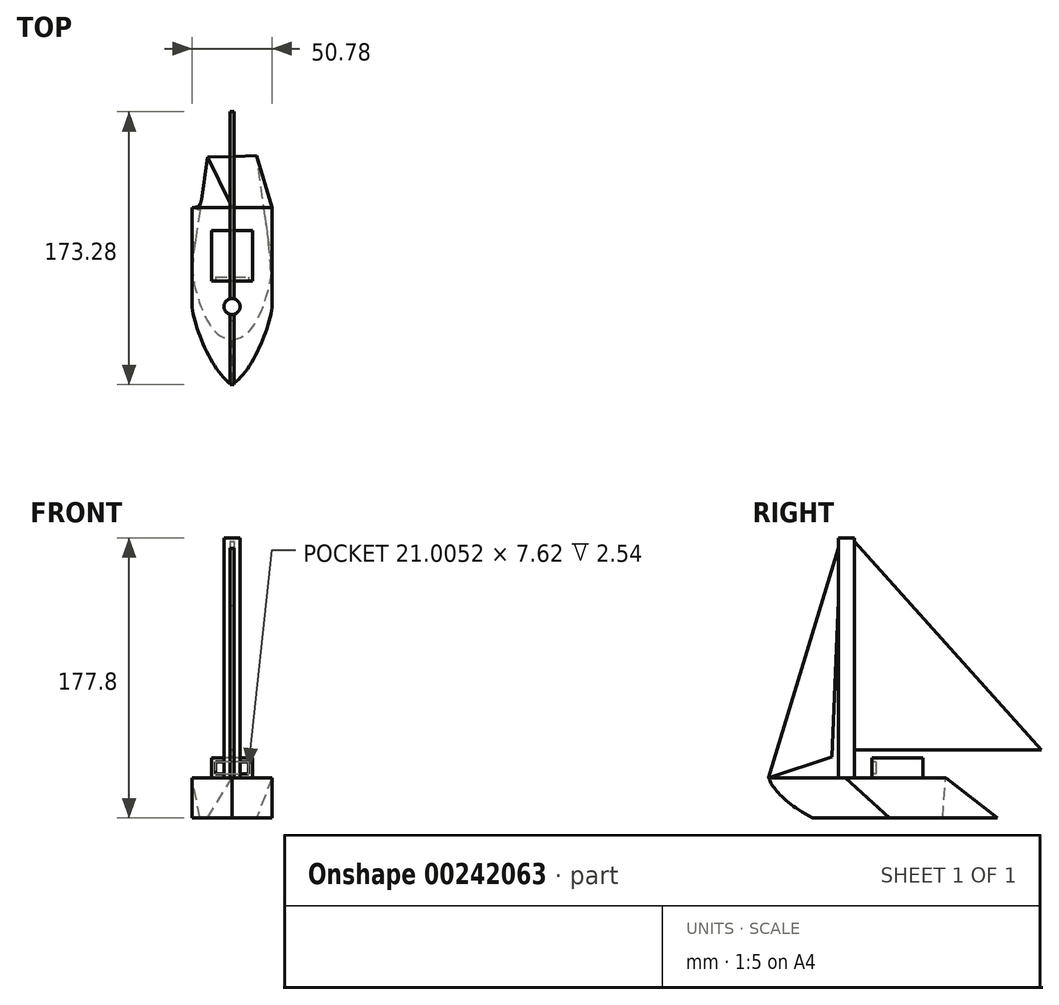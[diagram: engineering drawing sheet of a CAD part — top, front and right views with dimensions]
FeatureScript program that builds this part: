
annotation { "Feature Type Name" : "Feature", "Feature Type Description" : "" }
export const myFeature = defineFeature(function(context is Context, id is Id, definition is map)
    precondition{}
    {
        {
            var Q0;
            Q0=qCreatedBy(makeId("Top.planeOp"),FACE);
            var sketch = newSketch(context, id + "F0", { "sketchPlane" : qUnion([Q0])});
            skLineSegment(sketch, "E0", {"start": v(0, 46.92) * mm, "end": v(-25.39, 46.92) * mm});
            skLineSegment(sketch, "E1", {"start": v(-25.39, 46.92) * mm, "end": v(-25.39, -16.69) * mm});
            skFitSpline(sketch, "E2", {"points": [v(-25.39, -16.69) * mm, v(0, -65.46) * mm], "startDerivative": vector(6, -46.2) * mm, "endDerivative": vector(34.23, -18.83) * mm});
            skFitSpline(sketch, "E3.MirrorCS", {"points": [v(25.39, -16.69) * mm, v(0, -65.46) * mm], "startDerivative": vector(-6, -46.2) * mm, "endDerivative": vector(-34.23, -18.83) * mm});
            skLineSegment(sketch, "E4.MirrorCS", {"start": v(0, 46.92) * mm, "end": v(25.39, 46.92) * mm});
            skLineSegment(sketch, "E5.MirrorCS", {"start": v(25.39, 46.92) * mm, "end": v(25.39, -16.69) * mm});
            skSolve(sketch);
        }
        {
            var Q0;
            Q0=qCreatedBy(makeId("Top.planeOp"),FACE);
            cPlane(context, id + "F1", {"entities" : qUnion([Q0]), "cplaneType" : CPlaneType.OFFSET, "offset" : 25.4 * mm, "oppositeDirection" : true, "width" : 152.4 * mm, "height" : 152.4 * mm});
        }
        {
            var Q0;
            Q0=qCreatedBy(id+"F1.planeOp",FACE);
            var sketch = newSketch(context, id + "F2", { "sketchPlane" : qUnion([Q0])});
            skLineSegment(sketch, "E6.0.0", {"start": v(25.39, 11.24) * mm, "end": v(15.62, 79.73) * mm});
            skLineSegment(sketch, "E6.0.3", {"start": v(-15.47, 78.88) * mm, "end": v(-25.39, 11.24) * mm});
            skFitSpline(sketch, "E6.0.4", {"points": [v(-25.39, 11.24) * mm, v(-23.39, -4.17) * mm, v(-11.4, -31.26) * mm, v(0, -37.54) * mm]});
            skFitSpline(sketch, "E6.0.5", {"points": [v(0, -37.54) * mm, v(11.4, -31.26) * mm, v(23.39, -4.17) * mm, v(25.39, 11.24) * mm]});
            skLineSegment(sketch, "E7", {"start": v(-15.47, 78.88) * mm, "end": v(15.62, 79.73) * mm});
            skSolve(sketch);
        }
        {
            var Q0;
            Q0=qCreatedBy(makeId("Right.planeOp"),FACE);
            var sketch = newSketch(context, id + "F3", { "sketchPlane" : qUnion([Q0])});
            skFitSpline(sketch, "E8", {"points": [v(-65.46, 0) * mm, v(-37.54, -25.4) * mm], "startDerivative": vector(6, -17.03) * mm, "endDerivative": vector(55.16, -28.17) * mm});
            skSolve(sketch);
        }
        {
            var Q0;
            Q0=sQuery(id+"F0.wireOp",VERTEX,"E5.MirrorCS.start");
            var Q1;
            Q1=sQuery(id+"F2.wireOp",VERTEX,"E6.0.0.end");
            var Q2;
            Q2=sQuery(id+"F0.wireOp",VERTEX,"E0.end");
            cPlane(context, id + "F4", {"entities" : qUnion([Q0, Q1, Q2]), "cplaneType" : CPlaneType.THREE_POINT, "offset" : 25.4 * mm, "width" : 152.4 * mm, "height" : 152.4 * mm});
        }
        {
            var Q0;
            Q0=qCreatedBy(id+"F4.planeOp",FACE);
            var sketch = newSketch(context, id + "F5", { "sketchPlane" : qUnion([Q0])});
            skLineSegment(sketch, "E9", {"start": v(25.39, -37.1) * mm, "end": v(15.62, -78.6) * mm});
            skSolve(sketch);
        }
        {
            var Q0;
            Q0=makeQuery(id+"F2.imprint","IMPRINT",FACE,{"disambiguationData":[TD([[makeQuery(id+"F2.imprint","IMPRINT",EDGE,{"derivedFrom":sQuery(id+"F2.wireOp",EDGE,"E6.0.0")}),1.0]])]});
            var Q1;
            Q1=makeQuery(id+"F0.imprint","IMPRINT",FACE,{"disambiguationData":[TD([[makeQuery(id+"F0.imprint","IMPRINT",EDGE,{"derivedFrom":sQuery(id+"F0.wireOp",EDGE,"E0")}),1.0]])]});
            var Q2;
            Q2=sQuery(id+"F5.wireOp",EDGE,"E9");
            var Q3;
            Q3=sQuery(id+"F3.wireOp",EDGE,"E8");
            loft(context, id + "F6", {"addGuides" : true, "sheetProfilesArray" : [{ "sheetProfileEntities" : qUnion([Q0]) }, { "sheetProfileEntities" : qUnion([Q1]) }], "guidesArray" : [{ "guideEntities" : qUnion([Q2]), "guideDerivativeType" : LoftGuideDerivativeType.DEFAULT, "guideDerivativeMagnitude" : 1 }, { "guideEntities" : qUnion([Q3]), "guideDerivativeType" : LoftGuideDerivativeType.DEFAULT, "guideDerivativeMagnitude" : 1 }]});
        }
        {
            var Q0;
            Q0=makeQuery(id+"F6.opLoft","CAP_FACE",FACE,{"disambiguationData":[OSD([makeQuery(id+"F0.imprint","IMPRINT",FACE,{"disambiguationData":[TD([[makeQuery(id+"F0.imprint","IMPRINT",EDGE,{"derivedFrom":sQuery(id+"F0.wireOp",EDGE,"E0")}),1.0]])]})])],"isStart":true});
            var sketch = newSketch(context, id + "F7", { "sketchPlane" : qUnion([Q0])});
            skSolve(sketch);
        }
        {
            var Q0;
            {var subQ5=sQuery(id+"F0.wireOp",EDGE,"E0");var subQ6=sQuery(id+"F5.wireOp",EDGE,"E9");Q0=makeQuery(id+"F7.imprint","IMPRINT",FACE,{"disambiguationData":[TD([[makeQuery(id+"F7.imprint","IMPRINT",EDGE,{"derivedFrom":makeQuery(id+"F6.opLoft","MID_CAP_EDGE",EDGE,{"disambiguationData":[OSD([subQ5,sQuery(id+"F0.wireOp",EDGE,"E4.MirrorCS"),subQ6])],"capPos":1.0})}),1.0]])]});}
            var sketch = newSketch(context, id + "F8", { "sketchPlane" : qUnion([Q0])});
            skLineSegment(sketch, "E10", {"start": v(0, 0) * mm, "end": v(-13.04, 0) * mm});
            skLineSegment(sketch, "E11", {"start": v(-13.04, 0) * mm, "end": v(-13.04, 32.38) * mm});
            skLineSegment(sketch, "E12", {"start": v(-13.04, 32.38) * mm, "end": v(0, 32.38) * mm});
            skLineSegment(sketch, "E13.MirrorCS", {"start": v(13.04, 0) * mm, "end": v(13.04, 32.38) * mm});
            skLineSegment(sketch, "E14.MirrorCS", {"start": v(13.04, 32.38) * mm, "end": v(0, 32.38) * mm});
            skLineSegment(sketch, "E15.MirrorCS", {"start": v(0, 0) * mm, "end": v(13.04, 0) * mm});
            skSolve(sketch);
        }
        {
            var Q0;
            Q0 = qSketchRegion(id + "F8", true);
            extrude(context, id + "F9", {"entities" : qUnion([Q0]), "operationType" : NewBodyOperationType.ADD, "depth" : 12.7 * mm});
        }
        {
            var Q0;
            {var subQ5=sQuery(id+"F0.wireOp",EDGE,"E0");var subQ6=sQuery(id+"F5.wireOp",EDGE,"E9");Q0=makeQuery(id+"F7.imprint","IMPRINT",FACE,{"disambiguationData":[TD([[makeQuery(id+"F7.imprint","IMPRINT",EDGE,{"derivedFrom":makeQuery(id+"F6.opLoft","MID_CAP_EDGE",EDGE,{"disambiguationData":[OSD([subQ5,sQuery(id+"F0.wireOp",EDGE,"E4.MirrorCS"),subQ6])],"capPos":1.0})}),1.0]])]});}
            var sketch = newSketch(context, id + "F10", { "sketchPlane" : qUnion([Q0])});
            skCircle(sketch, "E16", {"center": v(0, -16.07) * mm, "radius": 5.12 * mm});
            skSolve(sketch);
        }
        {
            var Q0;
            Q0=makeQuery(id+"F10.imprint","IMPRINT",FACE,{"disambiguationData":[TD([[makeQuery(id+"F10.imprint","IMPRINT",EDGE,{"derivedFrom":sQuery(id+"F10.wireOp",EDGE,"E16")}),1.0]])]});
            extrude(context, id + "F11", {"entities" : qUnion([Q0]), "operationType" : NewBodyOperationType.ADD, "depth" : 152.4 * mm});
        }
        {
            var Q0;
            Q0=qCreatedBy(makeId("Right.planeOp"),FACE);
            var sketch = newSketch(context, id + "F12", { "sketchPlane" : qUnion([Q0])});
            skLineSegment(sketch, "E17", {"start": v(-19.34, 151.7) * mm, "end": v(-25.33, 13.5) * mm});
            skLineSegment(sketch, "E18", {"start": v(-25.33, 13.5) * mm, "end": v(-65.55, 0) * mm});
            skLineSegment(sketch, "E19", {"start": v(-65.55, 0) * mm, "end": v(-19.34, 151.7) * mm});
            skLineSegment(sketch, "E20", {"start": v(-12.5, 151.7) * mm, "end": v(107.73, 17.78) * mm});
            skLineSegment(sketch, "E21", {"start": v(107.73, 17.78) * mm, "end": v(-11.21, 17.78) * mm});
            skLineSegment(sketch, "E22", {"start": v(-11.21, 17.78) * mm, "end": v(-12.5, 151.7) * mm});
            skSolve(sketch);
        }
        {
            var Q0;
            Q0=makeQuery(id+"F12.imprint","IMPRINT",FACE,{"disambiguationData":[TD([[makeQuery(id+"F12.imprint","IMPRINT",EDGE,{"derivedFrom":sQuery(id+"F12.wireOp",EDGE,"E17")}),-1.0]])]});
            var Q1;
            Q1=makeQuery(id+"F12.imprint","IMPRINT",FACE,{"disambiguationData":[TD([[makeQuery(id+"F12.imprint","IMPRINT",EDGE,{"derivedFrom":sQuery(id+"F12.wireOp",EDGE,"E20")}),-1.0]])]});
            extrude(context, id + "F13", {"entities" : qUnion([Q0, Q1]), "operationType" : NewBodyOperationType.ADD, "endBound" : BoundingType.SYMMETRIC, "depth" : 2.54 * mm});
        }
        {
            var Q0;
            Q0=makeQuery(id+"F9.opExtrude","SWEPT_FACE",FACE,{"disambiguationData":[OSD([sQuery(id+"F8.wireOp",EDGE,"E10"),sQuery(id+"F8.wireOp",EDGE,"E15.MirrorCS")])]});
            var sketch = newSketch(context, id + "F14", { "sketchPlane" : qUnion([Q0])});
            skLineSegment(sketch, "E23.0", {"start": v(-10.5, 2.54) * mm, "end": v(10.5, 2.54) * mm});
            skLineSegment(sketch, "E23.1", {"start": v(-10.5, 10.16) * mm, "end": v(-10.5, 2.54) * mm});
            skLineSegment(sketch, "E23.2", {"start": v(10.5, 10.16) * mm, "end": v(-10.5, 10.16) * mm});
            skLineSegment(sketch, "E23.3", {"start": v(10.5, 2.54) * mm, "end": v(10.5, 10.16) * mm});
            skSolve(sketch);
        }
        {
            var Q0;
            Q0=makeQuery(id+"F14.imprint","IMPRINT",FACE,{"disambiguationData":[TD([[makeQuery(id+"F14.imprint","IMPRINT",EDGE,{"derivedFrom":sQuery(id+"F14.wireOp",EDGE,"E23.0")}),1.0]])]});
            extrude(context, id + "F15", {"entities" : qUnion([Q0]), "operationType" : NewBodyOperationType.REMOVE, "oppositeDirection" : true, "depth" : 2.54 * mm});
        }
    });
